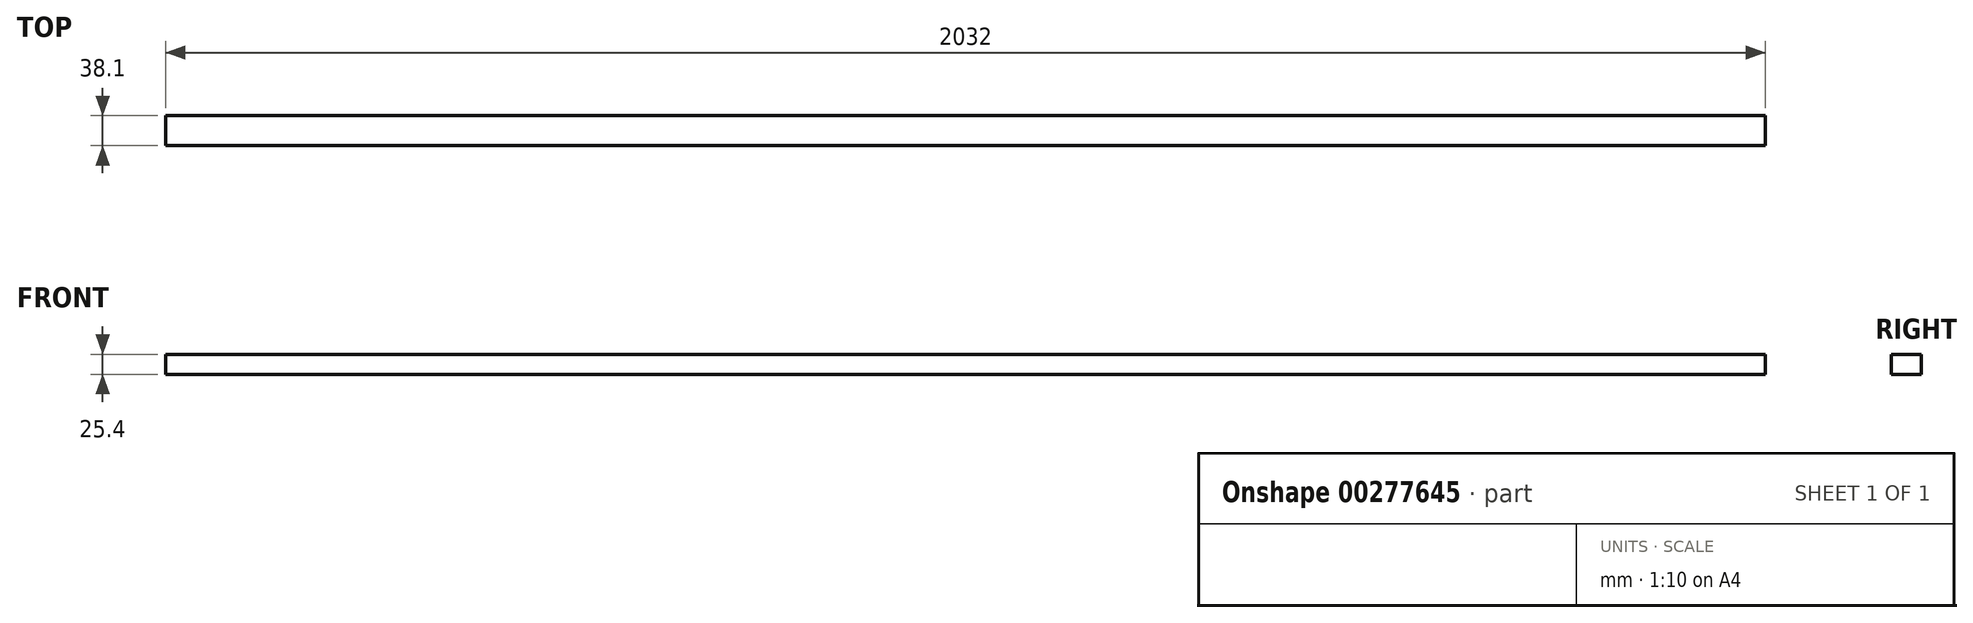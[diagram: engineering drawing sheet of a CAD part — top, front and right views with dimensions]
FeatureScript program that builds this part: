
annotation { "Feature Type Name" : "Feature", "Feature Type Description" : "" }
export const myFeature = defineFeature(function(context is Context, id is Id, definition is map)
    precondition{}
    {
        {
            var Q0;
            Q0=qCreatedBy(makeId("Front.planeOp"),FACE);
            var sketch = newSketch(context, id + "F0", { "sketchPlane" : qUnion([Q0])});
            skLineSegment(sketch, "E0.bottom", {"start": v(1016, 12.7) * mm, "end": v(-1016, 12.7) * mm});
            skLineSegment(sketch, "E0.top", {"start": v(1016, -12.7) * mm, "end": v(-1016, -12.7) * mm});
            skLineSegment(sketch, "E0.left", {"start": v(1016, 12.7) * mm, "end": v(1016, -12.7) * mm});
            skLineSegment(sketch, "E0.right", {"start": v(-1016, 12.7) * mm, "end": v(-1016, -12.7) * mm});
            skPoint(sketch, "E0.middle", {"position": v(0, 0) * mm});
            skSolve(sketch);
        }
        {
            var Q0;
            Q0 = qSketchRegion(id + "F0", true);
            extrude(context, id + "F1", {"entities" : qUnion([Q0]), "endBound" : BoundingType.SYMMETRIC, "depth" : 38.1 * mm});
        }
    });
